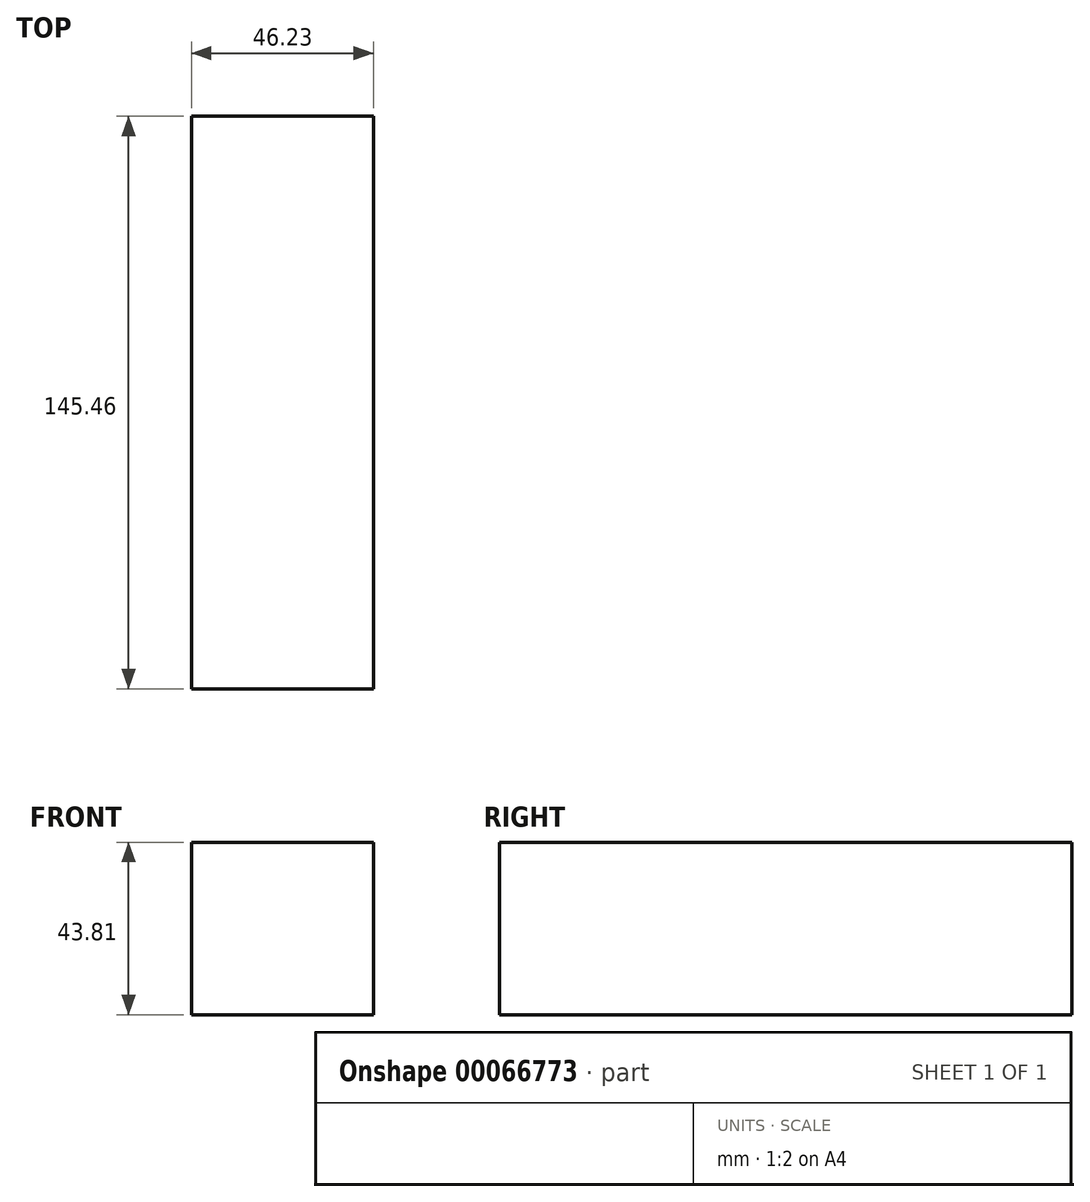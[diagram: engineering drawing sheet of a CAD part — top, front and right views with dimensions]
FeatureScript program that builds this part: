
annotation { "Feature Type Name" : "Feature", "Feature Type Description" : "" }
export const myFeature = defineFeature(function(context is Context, id is Id, definition is map)
    precondition{}
    {
        {
            var Q0;
            Q0=qCreatedBy(makeId("Front.planeOp"),FACE);
            var sketch = newSketch(context, id + "F0", { "sketchPlane" : qUnion([Q0])});
            skLineSegment(sketch, "E0.bottom", {"start": v(0, 0) * mm, "end": v(46.23, 0) * mm});
            skLineSegment(sketch, "E0.top", {"start": v(0, 43.81) * mm, "end": v(46.23, 43.81) * mm});
            skLineSegment(sketch, "E0.left", {"start": v(0, 0) * mm, "end": v(0, 43.81) * mm});
            skLineSegment(sketch, "E0.right", {"start": v(46.23, 0) * mm, "end": v(46.23, 43.81) * mm});
            skSolve(sketch);
        }
        {
            var Q0;
            Q0 = qSketchRegion(id + "F0", true);
            extrude(context, id + "F1", {"entities" : qUnion([Q0]), "depth" : 145.46 * mm});
        }
    });
